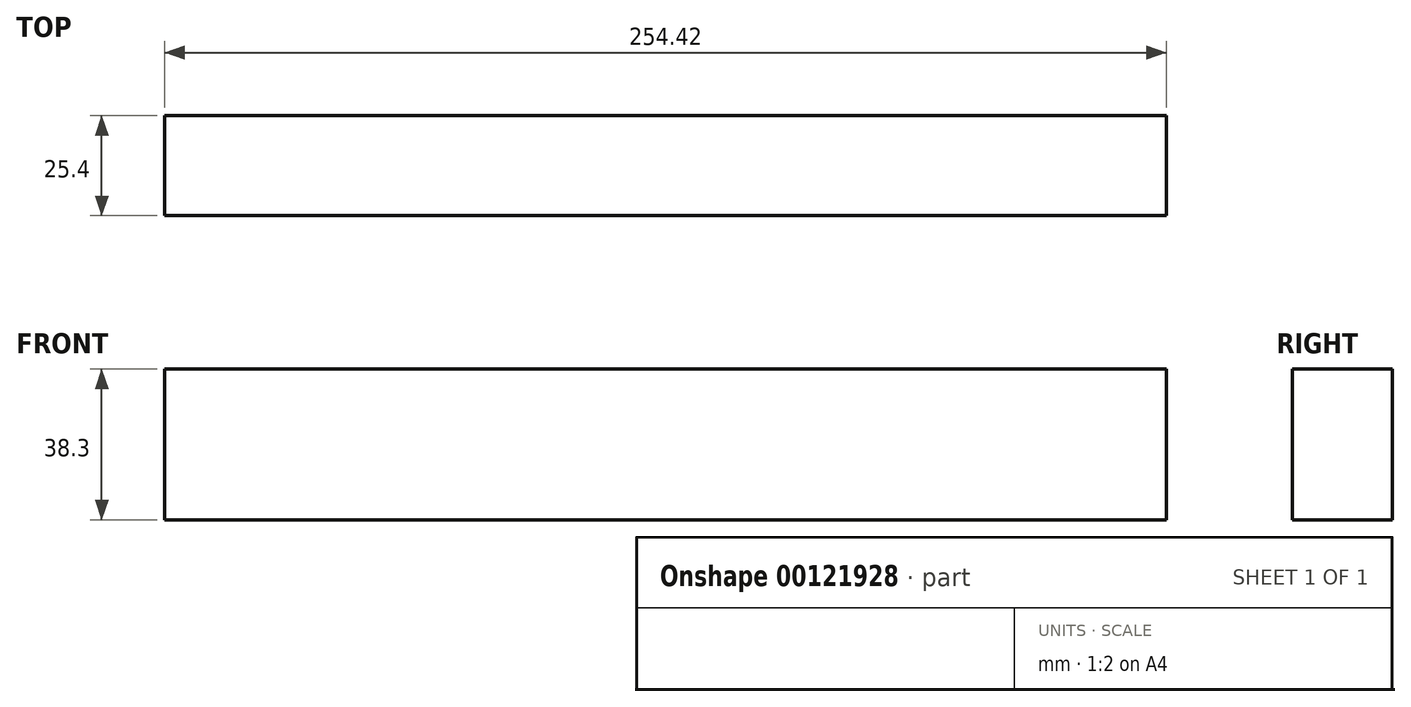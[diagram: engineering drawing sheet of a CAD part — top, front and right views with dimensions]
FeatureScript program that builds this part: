
annotation { "Feature Type Name" : "Feature", "Feature Type Description" : "" }
export const myFeature = defineFeature(function(context is Context, id is Id, definition is map)
    precondition{}
    {
        {
            var Q0;
            Q0=qCreatedBy(makeId("Front.planeOp"),FACE);
            var sketch = newSketch(context, id + "F0", { "sketchPlane" : qUnion([Q0])});
            skLineSegment(sketch, "E0.bottom", {"start": v(-129.86, 30.53) * mm, "end": v(124.56, 30.53) * mm});
            skLineSegment(sketch, "E0.top", {"start": v(-129.86, -7.77) * mm, "end": v(124.56, -7.77) * mm});
            skLineSegment(sketch, "E0.left", {"start": v(-129.86, 30.53) * mm, "end": v(-129.86, -7.77) * mm});
            skLineSegment(sketch, "E0.right", {"start": v(124.56, 30.53) * mm, "end": v(124.56, -7.77) * mm});
            skSolve(sketch);
        }
        {
            var Q0;
            Q0 = qSketchRegion(id + "F0", true);
            extrude(context, id + "F1", {"entities" : qUnion([Q0]), "depth" : 25.4 * mm});
        }
    });
